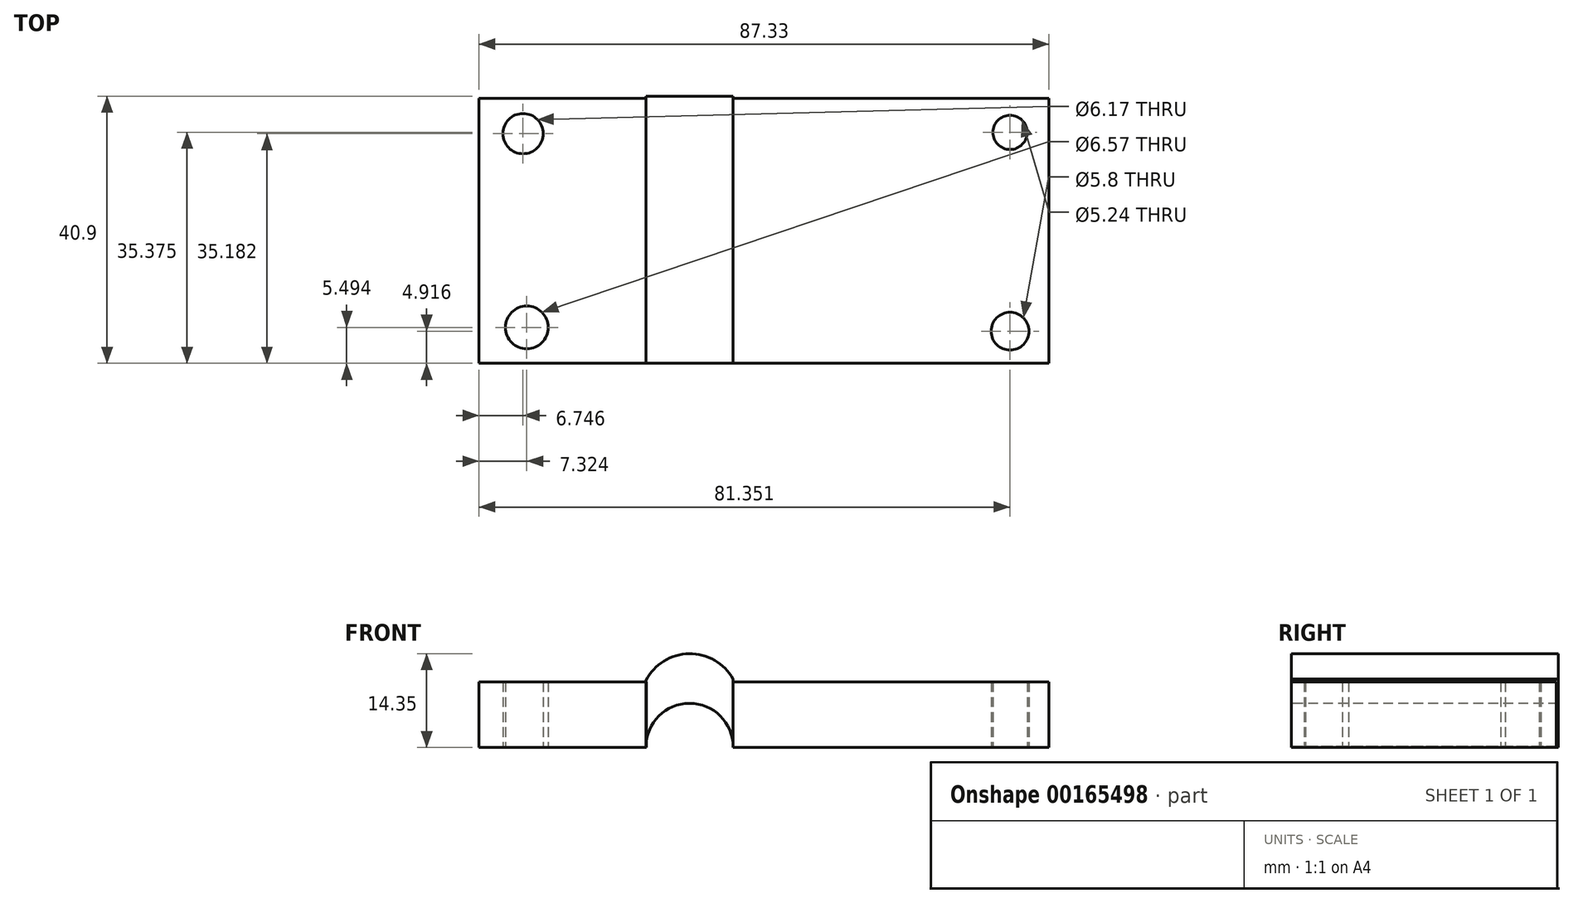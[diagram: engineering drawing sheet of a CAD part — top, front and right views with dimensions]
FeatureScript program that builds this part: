
annotation { "Feature Type Name" : "Feature", "Feature Type Description" : "" }
export const myFeature = defineFeature(function(context is Context, id is Id, definition is map)
    precondition{}
    {
        {
            var Q0;
            Q0=qCreatedBy(makeId("Top.planeOp"),FACE);
            var sketch = newSketch(context, id + "F0", { "sketchPlane" : qUnion([Q0])});
            skLineSegment(sketch, "E0.bottom", {"start": v(-38.94, 0) * mm, "end": v(48.39, 0) * mm});
            skLineSegment(sketch, "E0.top", {"start": v(-38.94, 40.58) * mm, "end": v(48.39, 40.58) * mm});
            skLineSegment(sketch, "E0.left", {"start": v(-38.94, 0) * mm, "end": v(-38.94, 40.58) * mm});
            skLineSegment(sketch, "E0.right", {"start": v(48.39, 0) * mm, "end": v(48.39, 40.58) * mm});
            skCircle(sketch, "E1", {"center": v(-32.2, 35.18) * mm, "radius": 3.08 * mm});
            skCircle(sketch, "E2", {"center": v(42.41, 35.37) * mm, "radius": 2.62 * mm});
            skCircle(sketch, "E3", {"center": v(42.41, 4.92) * mm, "radius": 2.9 * mm});
            skCircle(sketch, "E4", {"center": v(-31.62, 5.5) * mm, "radius": 3.28 * mm});
            skLineSegment(sketch, "E5.bottom", {"start": v(-13.3, 40.58) * mm, "end": v(0, 40.58) * mm});
            skLineSegment(sketch, "E5.top", {"start": v(-13.3, 0) * mm, "end": v(0, 0) * mm});
            skLineSegment(sketch, "E5.left", {"start": v(-13.3, 40.58) * mm, "end": v(-13.3, 0) * mm});
            skLineSegment(sketch, "E5.right", {"start": v(0, 40.58) * mm, "end": v(0, 0) * mm});
            skSolve(sketch);
        }
        {
            var Q0;
            {var subQ0=sQuery(id+"F0.wireOp",EDGE,"E0.left");Q0=makeQuery(id+"F0.imprint","IMPRINT",FACE,{"disambiguationData":[TD([[makeQuery(id+"F0.imprint","IMPRINT",EDGE,{"derivedFrom":subQ0}),-1.0]])]});}
            var Q1;
            {var subQ0=sQuery(id+"F0.wireOp",EDGE,"E0.right");Q1=makeQuery(id+"F0.imprint","IMPRINT",FACE,{"disambiguationData":[TD([[makeQuery(id+"F0.imprint","IMPRINT",EDGE,{"derivedFrom":subQ0}),1.0]])]});}
            extrude(context, id + "F1", {"entities" : qUnion([Q0, Q1]), "depth" : 10 * mm});
        }
        {
            var Q0;
            Q0=qCreatedBy(makeId("Front.planeOp"),FACE);
            var sketch = newSketch(context, id + "F2", { "sketchPlane" : qUnion([Q0])});
            skArc(sketch, "E6", {"start": v(0, 10.49) * mm, "mid": v(-6.75, 14.35) * mm, "end": v(-13.36, 10.26) * mm});
            skArc(sketch, "E7", {"start": v(0, 0) * mm, "mid": v(-6.68, 6.75) * mm, "end": v(-13.36, 0) * mm});
            skLineSegment(sketch, "E8", {"start": v(-13.36, 10.26) * mm, "end": v(-13.36, 0) * mm});
            skLineSegment(sketch, "E9", {"start": v(0, 10.49) * mm, "end": v(0, 0) * mm});
            skSolve(sketch);
        }
        {
            var Q0;
            Q0 = qSketchRegion(id + "F2", true);
            extrude(context, id + "F3", {"entities" : qUnion([Q0]), "oppositeDirection" : true, "depth" : 40.9 * mm});
        }
    });
